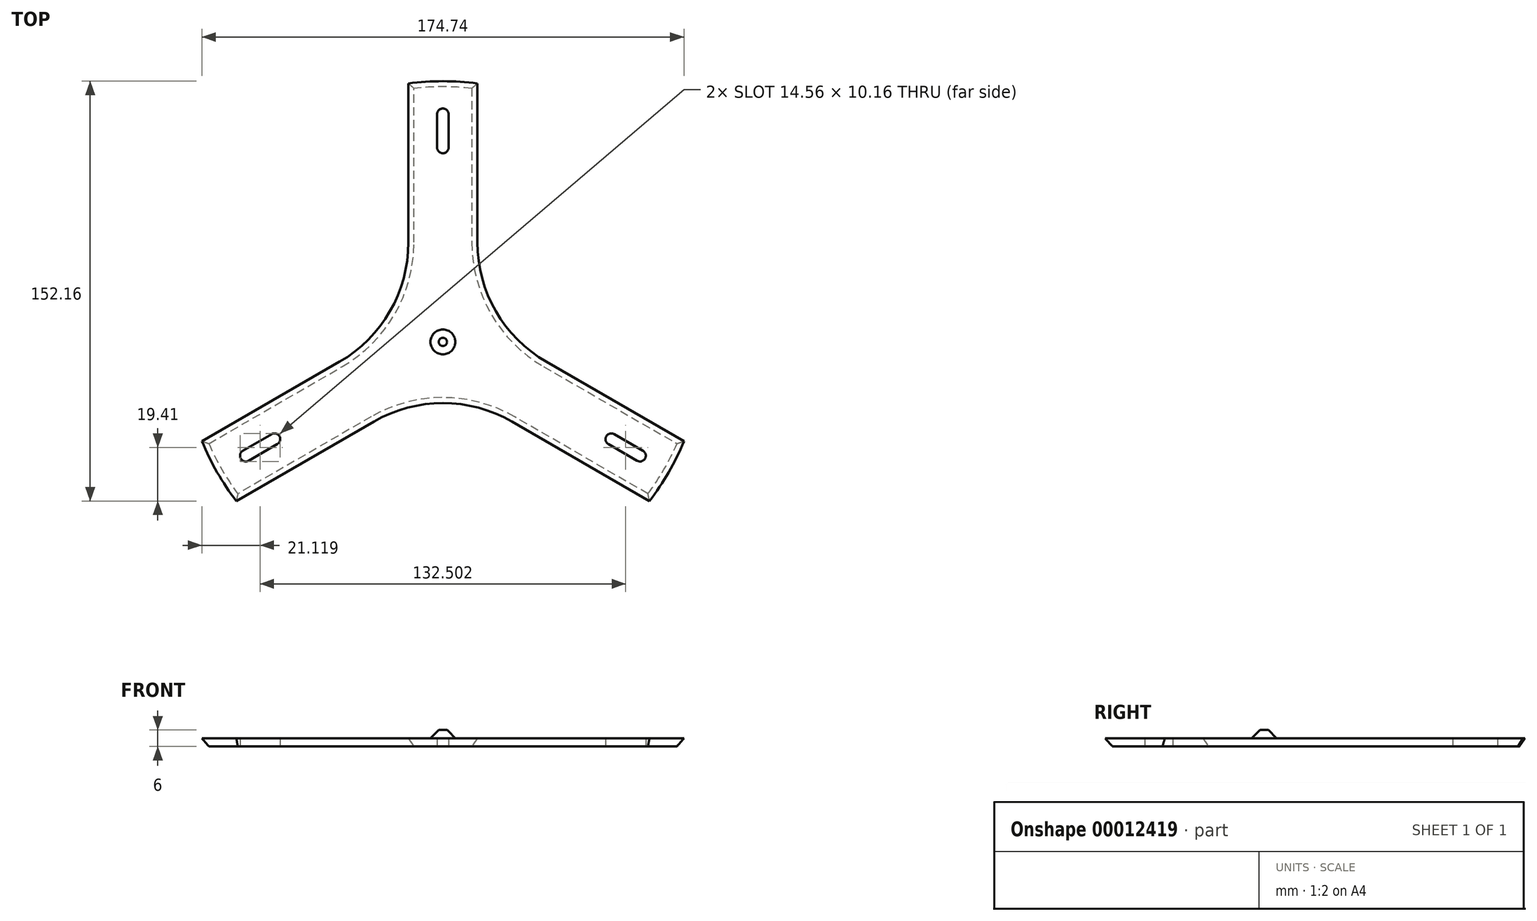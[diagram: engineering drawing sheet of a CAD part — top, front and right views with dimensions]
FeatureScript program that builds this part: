
annotation { "Feature Type Name" : "Feature", "Feature Type Description" : "" }
export const myFeature = defineFeature(function(context is Context, id is Id, definition is map)
    precondition{}
    {
        {
            var Q0;
            Q0=qCreatedBy(makeId("Top.planeOp"),FACE);
            var sketch = newSketch(context, id + "F0", { "sketchPlane" : qUnion([Q0])});
            skArc(sketch, "E0", {"start": v(12.5, 93.67) * mm, "mid": v(0, 94.5) * mm, "end": v(-12.5, 93.67) * mm});
            skCircle(sketch, "E1", {"center": v(0, 0) * mm, "radius": 76.5 * mm, "construction": true});
            skLineSegment(sketch, "E2", {"start": v(0, 0) * mm, "end": v(0, 94.5) * mm, "construction": true});
            skArc(sketch, "E3", {"start": v(-2.1, 70.5) * mm, "mid": v(0, 68.4) * mm, "end": v(2.1, 70.5) * mm});
            skArc(sketch, "E4", {"start": v(2.1, 82.5) * mm, "mid": v(0, 84.6) * mm, "end": v(-2.1, 82.5) * mm});
            skLineSegment(sketch, "E5", {"start": v(-2.1, 82.5) * mm, "end": v(-2.1, 70.5) * mm});
            skLineSegment(sketch, "E6", {"start": v(2.1, 82.5) * mm, "end": v(2.1, 70.5) * mm});
            skLineSegment(sketch, "E7.1.0", {"start": v(0, 0) * mm, "end": v(-81.84, 47.25) * mm, "construction": true});
            skLineSegment(sketch, "E7.2.0", {"start": v(0, 0) * mm, "end": v(-81.84, -47.25) * mm, "construction": true});
            skLineSegment(sketch, "E7.3.0", {"start": v(0, 0) * mm, "end": v(0, -94.5) * mm, "construction": true});
            skLineSegment(sketch, "E7.4.0", {"start": v(0, 0) * mm, "end": v(81.84, -47.25) * mm, "construction": true});
            skLineSegment(sketch, "E7.5.0", {"start": v(0, 0) * mm, "end": v(81.84, 47.25) * mm, "construction": true});
            skLineSegment(sketch, "E8", {"start": v(-12.5, 93.67) * mm, "end": v(-12.5, 7.22) * mm});
            skLineSegment(sketch, "E9.0.MirrorCS", {"start": v(12.5, 93.67) * mm, "end": v(12.5, 7.22) * mm});
            skArc(sketch, "E10.1.0", {"start": v(-87.37, -36) * mm, "mid": v(-81.84, -47.25) * mm, "end": v(-74.87, -57.66) * mm});
            skLineSegment(sketch, "E10.1.1", {"start": v(-87.37, -36) * mm, "end": v(-12.5, 7.22) * mm});
            skLineSegment(sketch, "E10.1.2", {"start": v(-74.87, -57.66) * mm, "end": v(0, -14.43) * mm});
            skLineSegment(sketch, "E10.1.3", {"start": v(-70.4, -43.07) * mm, "end": v(-60, -37.07) * mm});
            skLineSegment(sketch, "E10.1.4", {"start": v(-72.5, -39.43) * mm, "end": v(-62.1, -33.43) * mm});
            skArc(sketch, "E10.1.5", {"start": v(-72.5, -39.43) * mm, "mid": v(-73.27, -42.3) * mm, "end": v(-70.4, -43.07) * mm});
            skArc(sketch, "E10.1.6", {"start": v(-60, -37.07) * mm, "mid": v(-59.24, -34.2) * mm, "end": v(-62.1, -33.43) * mm});
            skArc(sketch, "E10.2.0", {"start": v(74.87, -57.66) * mm, "mid": v(81.84, -47.25) * mm, "end": v(87.37, -36) * mm});
            skLineSegment(sketch, "E10.2.1", {"start": v(74.87, -57.66) * mm, "end": v(0, -14.43) * mm});
            skLineSegment(sketch, "E10.2.2", {"start": v(87.37, -36) * mm, "end": v(12.5, 7.22) * mm});
            skLineSegment(sketch, "E10.2.3", {"start": v(72.5, -39.43) * mm, "end": v(62.1, -33.43) * mm});
            skLineSegment(sketch, "E10.2.4", {"start": v(70.4, -43.07) * mm, "end": v(60, -37.07) * mm});
            skArc(sketch, "E10.2.5", {"start": v(70.4, -43.07) * mm, "mid": v(73.27, -42.3) * mm, "end": v(72.5, -39.43) * mm});
            skArc(sketch, "E10.2.6", {"start": v(62.1, -33.43) * mm, "mid": v(59.24, -34.2) * mm, "end": v(60, -37.07) * mm});
            skSolve(sketch);
        }
        {
            var Q0;
            Q0 = qSketchRegion(id + "F0", true);
            extrude(context, id + "F1", {"entities" : qUnion([Q0]), "depth" : 3 * mm});
        }
        {
            var Q0;
            Q0=makeQuery(id+"F1.opExtrude","CAP_FACE",FACE,{"disambiguationData":[OSD([sQuery(id+"F0.wireOp",EDGE,"E0"),sQuery(id+"F0.wireOp",EDGE,"E3"),sQuery(id+"F0.wireOp",EDGE,"E4"),sQuery(id+"F0.wireOp",EDGE,"E5"),sQuery(id+"F0.wireOp",EDGE,"E6"),sQuery(id+"F0.wireOp",EDGE,"E8"),sQuery(id+"F0.wireOp",EDGE,"E9.0.MirrorCS"),sQuery(id+"F0.wireOp",EDGE,"E10.1.0"),sQuery(id+"F0.wireOp",EDGE,"E10.1.1"),sQuery(id+"F0.wireOp",EDGE,"E10.1.2"),sQuery(id+"F0.wireOp",EDGE,"E10.1.3"),sQuery(id+"F0.wireOp",EDGE,"E10.1.4"),sQuery(id+"F0.wireOp",EDGE,"E10.1.5"),sQuery(id+"F0.wireOp",EDGE,"E10.1.6"),sQuery(id+"F0.wireOp",EDGE,"E10.2.0"),sQuery(id+"F0.wireOp",EDGE,"E10.2.1"),sQuery(id+"F0.wireOp",EDGE,"E10.2.2"),sQuery(id+"F0.wireOp",EDGE,"E10.2.3"),sQuery(id+"F0.wireOp",EDGE,"E10.2.4"),sQuery(id+"F0.wireOp",EDGE,"E10.2.5"),sQuery(id+"F0.wireOp",EDGE,"E10.2.6")])],"isStart":false});
            var sketch = newSketch(context, id + "F2", { "sketchPlane" : qUnion([Q0])});
            skCircle(sketch, "E11", {"center": v(0, 0) * mm, "radius": 4.5 * mm});
            skSolve(sketch);
        }
        {
            var Q0;
            Q0 = qSketchRegion(id + "F2", true);
            extrude(context, id + "F3", {"entities" : qUnion([Q0]), "operationType" : NewBodyOperationType.ADD, "depth" : 3 * mm});
        }
        {
            var Q0;
            Q0=makeQuery(id+"F3.opExtrude","CAP_EDGE",EDGE,{"disambiguationData":[OSD([sQuery(id+"F2.wireOp",EDGE,"E11")])],"isStart":false});
            chamfer(context, id + "F4", {"entities" : qUnion([Q0]), "width" : 3 * mm, "tangentPropagation" : true});
        }
        {
            var Q0;
            Q0=makeQuery(id+"F1.opExtrude","CAP_EDGE",EDGE,{"disambiguationData":[OSD([sQuery(id+"F0.wireOp",EDGE,"E10.1.0")])],"isStart":true});
            var Q1;
            Q1=makeQuery(id+"F1.opExtrude","CAP_EDGE",EDGE,{"disambiguationData":[OSD([sQuery(id+"F0.wireOp",EDGE,"E10.2.0")])],"isStart":true});
            var Q2;
            Q2=makeQuery(id+"F1.opExtrude","CAP_EDGE",EDGE,{"disambiguationData":[OSD([sQuery(id+"F0.wireOp",EDGE,"E0")])],"isStart":true});
            chamfer(context, id + "F5", {"entities" : qUnion([Q0, Q1, Q2]), "chamferType" : ChamferType.TWO_OFFSETS, "width1" : 3 * mm, "oppositeDirection" : false, "width2" : 2 * mm, "tangentPropagation" : true});
        }
        {
            var Q0;
            Q0=makeQuery(id+"F1.opExtrude","SWEPT_EDGE",EDGE,{"disambiguationData":[OSD([sQuery(id+"F0.wireOp",EDGE,"E8"),sQuery(id+"F0.wireOp",EDGE,"E10.1.1")])]});
            var Q1;
            Q1=makeQuery(id+"F1.opExtrude","SWEPT_EDGE",EDGE,{"disambiguationData":[OSD([sQuery(id+"F0.wireOp",EDGE,"E10.1.2"),sQuery(id+"F0.wireOp",EDGE,"E10.2.1")])]});
            var Q2;
            Q2=makeQuery(id+"F1.opExtrude","SWEPT_EDGE",EDGE,{"disambiguationData":[OSD([sQuery(id+"F0.wireOp",EDGE,"E9.0.MirrorCS"),sQuery(id+"F0.wireOp",EDGE,"E10.2.2")])]});
            fillet(context, id + "F6", {"entities" : qUnion([Q0, Q1, Q2]), "radius" : 50 * mm, "tangentPropagation" : true, "allowEdgeOverflow" : false});
        }
        {
            var Q0;
            Q0=makeQuery(id+"F1.opExtrude","CAP_EDGE",EDGE,{"disambiguationData":[OSD([sQuery(id+"F0.wireOp",EDGE,"E10.2.1")])],"isStart":true});
            var Q1;
            Q1=makeQuery(id+"F1.opExtrude","CAP_EDGE",EDGE,{"disambiguationData":[OSD([sQuery(id+"F0.wireOp",EDGE,"E10.2.2")])],"isStart":true});
            var Q2;
            {var subQ0=sQuery(id+"F0.wireOp",EDGE,"E8");var subQ1=sQuery(id+"F0.wireOp",EDGE,"E10.1.1");Q2=makeQuery(id+"F6.opFillet","BLEND_EDGE",EDGE,{"blendedFrom":[makeQuery(id+"F1.opExtrude","SWEPT_EDGE",EDGE,{"disambiguationData":[OSD([subQ0,subQ1])]}),makeQuery(id+"F1.opExtrude","CAP_FACE",FACE,{"disambiguationData":[OSD([sQuery(id+"F0.wireOp",EDGE,"E0"),sQuery(id+"F0.wireOp",EDGE,"E3"),sQuery(id+"F0.wireOp",EDGE,"E4"),sQuery(id+"F0.wireOp",EDGE,"E5"),sQuery(id+"F0.wireOp",EDGE,"E6"),subQ0,sQuery(id+"F0.wireOp",EDGE,"E9.0.MirrorCS"),sQuery(id+"F0.wireOp",EDGE,"E10.1.0"),subQ1,sQuery(id+"F0.wireOp",EDGE,"E10.1.2"),sQuery(id+"F0.wireOp",EDGE,"E10.1.3"),sQuery(id+"F0.wireOp",EDGE,"E10.1.4"),sQuery(id+"F0.wireOp",EDGE,"E10.1.5"),sQuery(id+"F0.wireOp",EDGE,"E10.1.6"),sQuery(id+"F0.wireOp",EDGE,"E10.2.0"),sQuery(id+"F0.wireOp",EDGE,"E10.2.1"),sQuery(id+"F0.wireOp",EDGE,"E10.2.2"),sQuery(id+"F0.wireOp",EDGE,"E10.2.3"),sQuery(id+"F0.wireOp",EDGE,"E10.2.4"),sQuery(id+"F0.wireOp",EDGE,"E10.2.5"),sQuery(id+"F0.wireOp",EDGE,"E10.2.6")])],"isStart":true})],"blendedInto":[makeQuery(id+"F1.opExtrude","CAP_FACE",FACE,{"disambiguationData":[OSD([sQuery(id+"F0.wireOp",EDGE,"E0"),sQuery(id+"F0.wireOp",EDGE,"E3"),sQuery(id+"F0.wireOp",EDGE,"E4"),sQuery(id+"F0.wireOp",EDGE,"E5"),sQuery(id+"F0.wireOp",EDGE,"E6"),subQ0,sQuery(id+"F0.wireOp",EDGE,"E9.0.MirrorCS"),sQuery(id+"F0.wireOp",EDGE,"E10.1.0"),subQ1,sQuery(id+"F0.wireOp",EDGE,"E10.1.2"),sQuery(id+"F0.wireOp",EDGE,"E10.1.3"),sQuery(id+"F0.wireOp",EDGE,"E10.1.4"),sQuery(id+"F0.wireOp",EDGE,"E10.1.5"),sQuery(id+"F0.wireOp",EDGE,"E10.1.6"),sQuery(id+"F0.wireOp",EDGE,"E10.2.0"),sQuery(id+"F0.wireOp",EDGE,"E10.2.1"),sQuery(id+"F0.wireOp",EDGE,"E10.2.2"),sQuery(id+"F0.wireOp",EDGE,"E10.2.3"),sQuery(id+"F0.wireOp",EDGE,"E10.2.4"),sQuery(id+"F0.wireOp",EDGE,"E10.2.5"),sQuery(id+"F0.wireOp",EDGE,"E10.2.6")])],"isStart":true})]});}
            chamfer(context, id + "F7", {"entities" : qUnion([Q0, Q1, Q2]), "chamferType" : ChamferType.TWO_OFFSETS, "width1" : 2 * mm, "oppositeDirection" : false, "width2" : 3 * mm, "tangentPropagation" : true});
        }
    });
